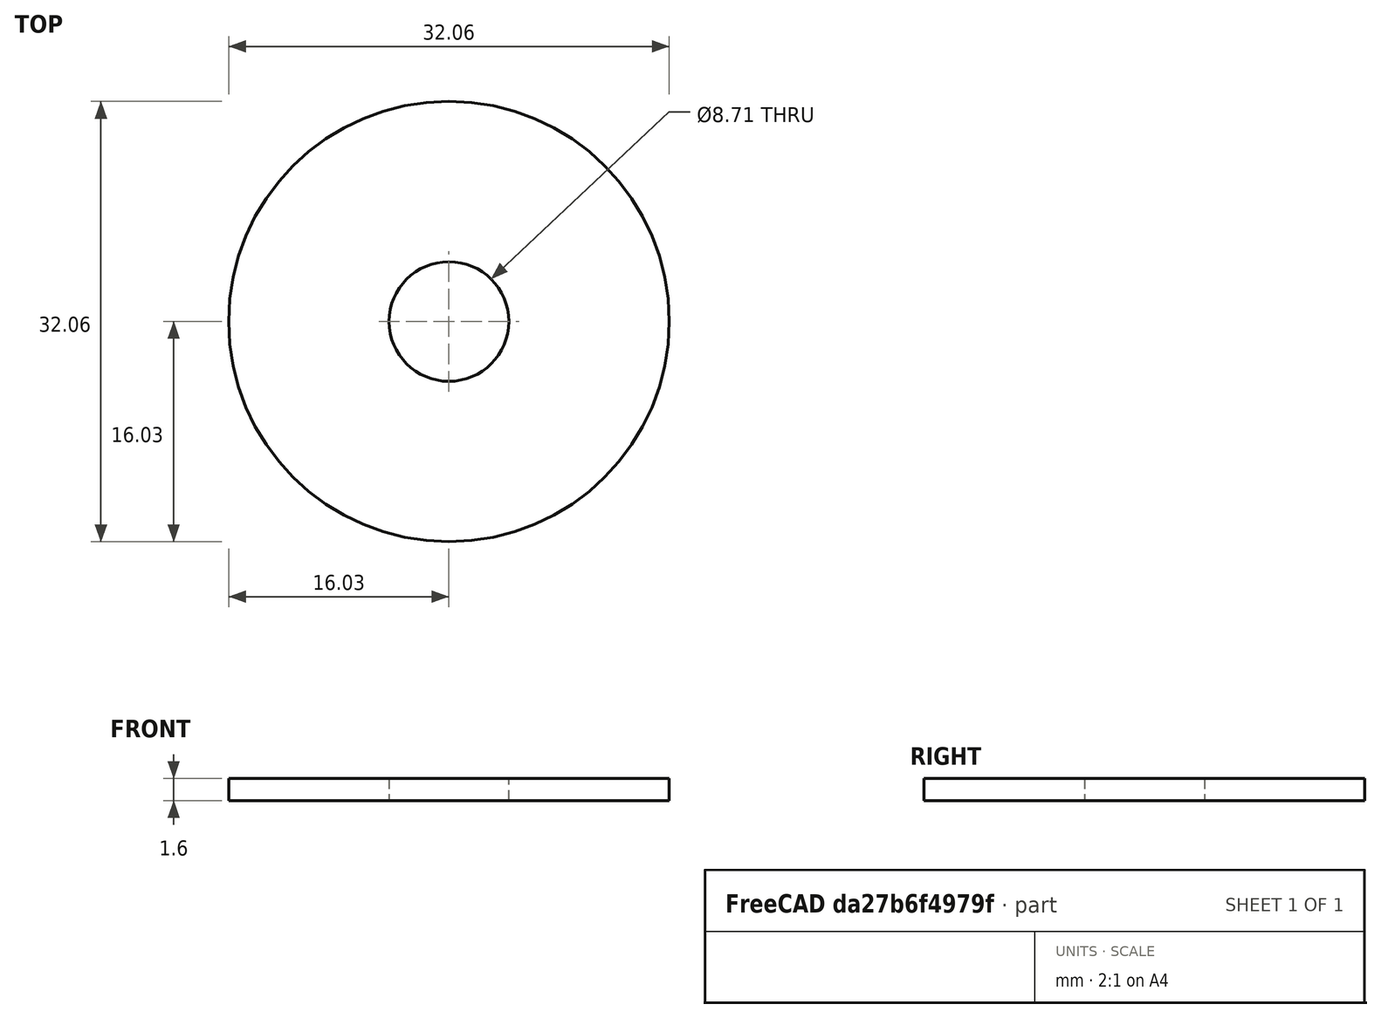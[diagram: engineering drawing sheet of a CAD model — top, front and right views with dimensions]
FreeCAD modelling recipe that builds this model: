
FCSTD DOCUMENT  (FreeCAD 1.1R40077 (Git))
Label: Washer
License: All rights reserved
LicenseURL: https://en.wikipedia.org/wiki/All_rights_reserved
objects: App::Point×1, Sketcher::SketchObject×1, PartDesign::Pad×1, PartDesign::Body×1, Measure::MeasureDistance×1, Measure::MeasureRadius×1, App::DocumentObjectGroup×1
note: 6 computed .brp shape members not serialized (recipe doc carries the construction recipe); baked Part::Feature solids carry a one-line shape summary decoded from their .brp

FEATURE [App::Point] Origin001
  Role = Origin
FEATURE [Sketcher::SketchObject] Sketch
  ArcFitTolerance = 1e-06
  AttachmentSupport = -> [XY_Plane]
  ExternalTypes = [0]
  FullyConstrained = true
  MakeInternals = false
  MapMode = 5
  expr: Constraints[3] = 32.06 mm
  sketch-geometry (2):
    g0: Circle CenterX=0 CenterY=0 CenterZ=0 NormalX=0 NormalY=0 NormalZ=1 AngleXU=0 Radius=4.355
    g1: Circle CenterX=0 CenterY=0 CenterZ=0 NormalX=0 NormalY=0 NormalZ=1 AngleXU=0 Radius=16.03
  constraints (4):
    c: Coincident(g0,g-1)
    c: Diameter(g0) = 8.71
    c: Coincident(g1,g0)
    c: Diameter(g1) = 32.06
FEATURE [PartDesign::Pad] Pad
  Direction = (0,0,1)
  Length = 1.6
  Length2 = 10
  Profile = -> Sketch
  ReferenceAxis = -> Sketch [N_Axis]
  Refine = true
  Suppressed = false
  Type = 0
FEATURE [PartDesign::Body] Body  label="Washer"
  AllowCompound = true
  Group = -> [Sketch,Pad]
  Origin = -> Origin
  Tip = -> Pad
FEATURE [Measure::MeasureDistance] Distance  label="Distance: 1.6000 mm"
  Distance = 1.6
  DistanceX = 0
  DistanceY = 0
  DistanceZ = 1.6
  Element1 = -> Body [Pad.Face4]
  Element2 = -> Body [Pad.Face3]
  Position1 = (16.03,0,1.6)
  Position2 = (16.03,0,0)
FEATURE [Measure::MeasureRadius] Radius  label="Radius: 16.0300 mm"
  Element = -> Body [Pad.Edge3]
  Radius = 16.03
FEATURE [App::DocumentObjectGroup] Measurements
  Group = -> [Distance,Radius]
